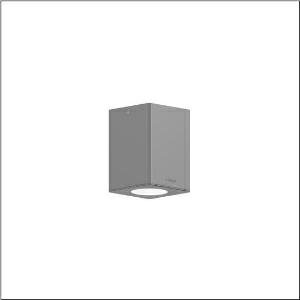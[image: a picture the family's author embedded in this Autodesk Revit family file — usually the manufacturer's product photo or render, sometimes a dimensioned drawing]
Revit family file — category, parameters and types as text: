
# Revit family: cl_31_decke_5cl613603
name_source: partatom
category: Lighting Fixtures
units: mm (PartAtom-declared; Revit-internal decimal feet)

## family parameters
Cut with Voids When Loaded = No
Host = Face
Light Source = No
Part Type = Normal
Room Calculation Point = No
Round Connector Dimension = Use Diameter
Shared = No

## types (1)
- --- (1 x LED, 1500 lm, 15 W, 3000K)
    Apparent Load = 15 VA
    CIE Flux Codes = 98 100 100 100 100
    Color Rendering = 80
    Color Temperature = 3000K
    Default Elevation = 1800 mm
    Description = CL 31 Ceiling, ceiling luminaire, primary light control with reflector, of aluminium, primary optical cover: cover panel, of glass, transparent, primary light characteristic: symmetric, installation type: surface-mounted, LED, rated luminous flux: 1.500lm, luminous efficacy: 100lm/W, light colour: 830, colour temperature: 3000K, control gear: ECG DALI, with terminal, 5-pole, max. 2.5mm², mains connection: 220..240V, AC, 50/60Hz, rated input power: 15W, luminaire housing, of aluminium, powder-coated, Siteco® metallic grey, length: 120mm, width: 120mm, height: 165mm, protection rating (complete): IP65, insulation class (complete): insulation class I (protective earthing), certification: CE, ENEC, impact resistance: IK09, permissible operating ambient temperature for outdoor applications: -20..+50°C, packaging unit: 1 piece
    Height = 166 mm
    Lamp = 1 x LED
    Lamp Light Flux = 1500 lm
    Lamp Power = 15 W
    Lamp count = 1
    Length = 120 mm
    Luminous efficacy = 100 lm/W
    Manufacturer = Siteco
    ModVariant = No
    Model = 5CL613603
    Mounting Place = Ceiling
    Mounting Type = Surface mounted
    Number of Poles = 1
    OnlyDefault = Yes
    Power Factor = 1
    Product Name = CL 31 Decke
    Product group = ceiling luminaire
    ProductGroupID = 305
    Protection Class = Protection class I
    Protection Degree = IP 65
    RLX_Detail_Level = 1
    RLX_Emergency_Light_Flux = 0 lm
    RLX_Emergency_Type = 0
    RLX_Emergency_Type_DB = No
    RlxData = <blob elided: 33173 chars, md5=e605f0e4>
    Socket = socket
    Standby Power = 0 W
    System Light Flux = 1500 lm
    System Power = 15 W
    Type Comments = factory setting: luminous flux: 100 % | dim-lin: 254 | 348 mA
    Type Image = l_1006909.jpg
    URL = http://relux.com
    VarID = @adj_130573
    Voltage = 0 V
    Weight = 0.00 kg
    Width = 120 mm

## geometry (parser evidence)
native form markers: Blend x4, Sweep x9
no freeform markers — native parametric forms only
